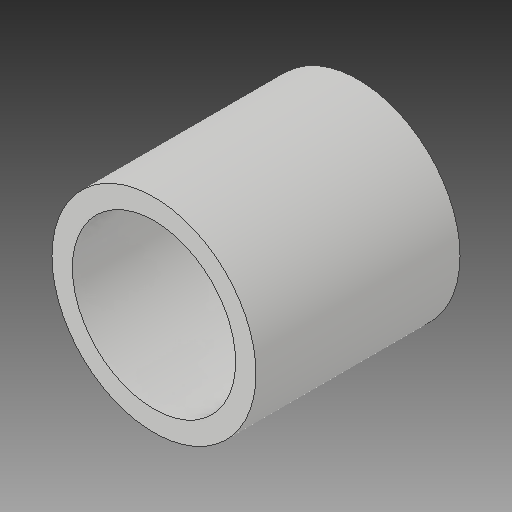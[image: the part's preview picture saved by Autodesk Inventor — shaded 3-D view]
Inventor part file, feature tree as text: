
AUTODESK INVENTOR PART (.ipt)
format: ipt  version: 2019 (Build 230136000, 136)  size: 107,008 bytes
history: native  units: mm
features: extrude x2, sketch x2
ambient origin geometry x8: Origin, YZ Plane, XZ Plane, XY Plane, X Axis, Y Axis, Z Axis, Center Point
bodies: Solid1 (feature_tree)
feature tree (4):
  extrude  "Extrusion1"  Depth=250.0mm TaperAngle=0.0deg
  extrude  "Extrusion2"  Depth=21.5mm TaperAngle=0.0deg
  sketch  "Sketch1"  dims[d0=250.0mm d1=250.0mm d2=0.0mm]
  sketch  "Sketch2"  dims[d3=200.0mm d4=21.5mm d5=0.0mm]
